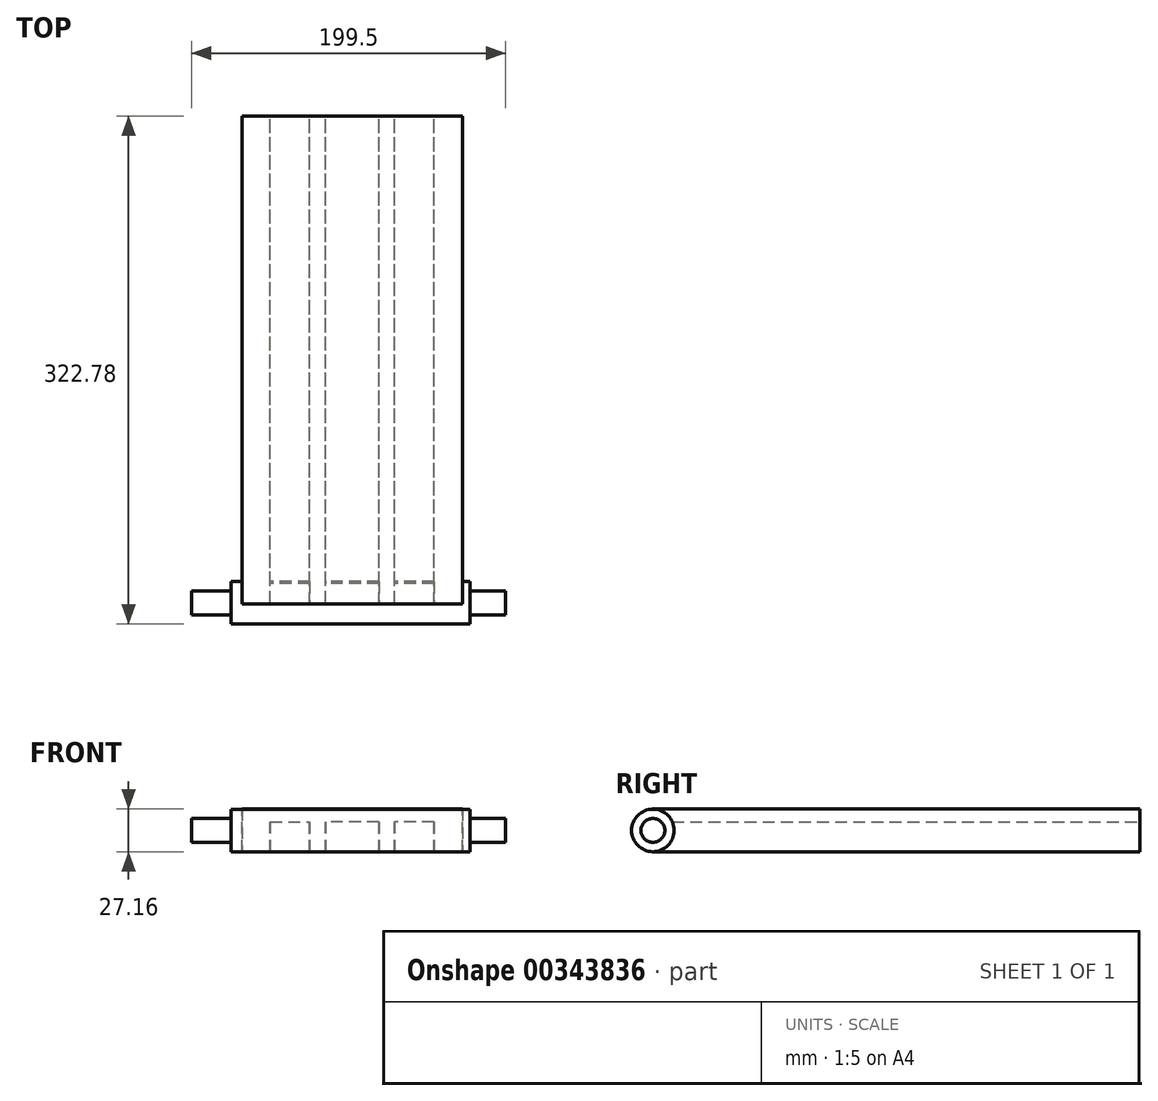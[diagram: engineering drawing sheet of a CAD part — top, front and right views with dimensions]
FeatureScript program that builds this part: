
annotation { "Feature Type Name" : "Feature", "Feature Type Description" : "" }
export const myFeature = defineFeature(function(context is Context, id is Id, definition is map)
    precondition{}
    {
        {
            var Q0;
            Q0=qCreatedBy(makeId("Front.planeOp"),FACE);
            var sketch = newSketch(context, id + "F0", { "sketchPlane" : qUnion([Q0])});
            skLineSegment(sketch, "E0.top", {"start": v(-51.02, -19.16) * mm, "end": v(-69.02, -19.16) * mm});
            skLineSegment(sketch, "E0.left", {"start": v(-51.02, 0) * mm, "end": v(-51.02, -19.16) * mm});
            skLineSegment(sketch, "E0.right", {"start": v(-69.02, 3.84) * mm, "end": v(-69.02, -19.16) * mm});
            skLineSegment(sketch, "E1.top", {"start": v(52.98, -19.16) * mm, "end": v(70.98, -19.16) * mm});
            skLineSegment(sketch, "E1.left", {"start": v(52.98, 0) * mm, "end": v(52.98, -19.16) * mm});
            skLineSegment(sketch, "E1.right", {"start": v(70.98, 3.84) * mm, "end": v(70.98, -19.16) * mm});
            skLineSegment(sketch, "E2.bottom", {"start": v(17.98, 0) * mm, "end": v(-16.02, 0) * mm});
            skLineSegment(sketch, "E3.top", {"start": v(-69.02, 8) * mm, "end": v(70.98, 8) * mm});
            skLineSegment(sketch, "E3.left", {"start": v(-69.02, 3.84) * mm, "end": v(-69.02, 8) * mm});
            skLineSegment(sketch, "E3.right", {"start": v(70.98, 3.84) * mm, "end": v(70.98, 8) * mm});
            skLineSegment(sketch, "E4.0", {"start": v(-26.02, 0) * mm, "end": v(-26.02, -19.16) * mm});
            skLineSegment(sketch, "E5.0", {"start": v(27.98, 0) * mm, "end": v(27.98, -19.16) * mm});
            skLineSegment(sketch, "E6.0", {"start": v(-16.02, 0) * mm, "end": v(-16.02, -19.16) * mm});
            skLineSegment(sketch, "E7.0", {"start": v(17.98, 0) * mm, "end": v(17.98, -19.16) * mm});
            skLineSegment(sketch, "E8", {"start": v(-16.02, -19.16) * mm, "end": v(-26.02, -19.16) * mm});
            skLineSegment(sketch, "E9", {"start": v(17.98, -19.16) * mm, "end": v(27.98, -19.16) * mm});
            skLineSegment(sketch, "E10", {"start": v(52.98, 0) * mm, "end": v(27.98, 0) * mm});
            skLineSegment(sketch, "E11", {"start": v(-51.02, 0) * mm, "end": v(-26.02, 0) * mm});
            skLineSegment(sketch, "E12", {"start": v(-51.02, 0) * mm, "end": v(-51.02, 8) * mm});
            skLineSegment(sketch, "E13", {"start": v(52.98, 0) * mm, "end": v(52.98, 8) * mm});
            skLineSegment(sketch, "E14", {"start": v(-26.02, 0) * mm, "end": v(-26.02, 8) * mm});
            skLineSegment(sketch, "E15", {"start": v(-16.02, 0) * mm, "end": v(-16.02, 8) * mm});
            skLineSegment(sketch, "E16", {"start": v(17.98, 0) * mm, "end": v(17.98, 8) * mm});
            skLineSegment(sketch, "E17", {"start": v(27.98, 0) * mm, "end": v(27.98, 8) * mm});
            skSolve(sketch);
        }
        {
            var Q0;
            Q0=makeQuery(id+"F0.imprint","IMPRINT",FACE,{"disambiguationData":[TD([[makeQuery(id+"F0.imprint","IMPRINT",EDGE,{"derivedFrom":sQuery(id+"F0.wireOp",EDGE,"E1.top")}),1.0]])]});
            var Q1;
            Q1=makeQuery(id+"F0.imprint","IMPRINT",FACE,{"disambiguationData":[TD([[makeQuery(id+"F0.imprint","IMPRINT",EDGE,{"derivedFrom":sQuery(id+"F0.wireOp",EDGE,"E0.top")}),-1.0]])]});
            extrude(context, id + "F1", {"entities" : qUnion([Q0, Q1]), "depth" : 310 * mm});
        }
        {
            var Q0;
            Q0=makeQuery(id+"F0.imprint","IMPRINT",FACE,{"disambiguationData":[TD([[makeQuery(id+"F0.imprint","IMPRINT",EDGE,{"derivedFrom":sQuery(id+"F0.wireOp",EDGE,"E2.bottom")}),-1.0]])]});
            extrude(context, id + "F2", {"entities" : qUnion([Q0]), "depth" : 250 * mm});
        }
        {
            var Q0;
            Q0=makeQuery(id+"F0.imprint","IMPRINT",FACE,{"disambiguationData":[TD([[makeQuery(id+"F0.imprint","IMPRINT",EDGE,{"derivedFrom":sQuery(id+"F0.wireOp",EDGE,"E4.0")}),1.0]])]});
            var Q1;
            Q1=makeQuery(id+"F0.imprint","IMPRINT",FACE,{"disambiguationData":[TD([[makeQuery(id+"F0.imprint","IMPRINT",EDGE,{"derivedFrom":sQuery(id+"F0.wireOp",EDGE,"E5.0")}),-1.0]])]});
            extrude(context, id + "F3", {"entities" : qUnion([Q0, Q1]), "operationType" : NewBodyOperationType.ADD, "depth" : 310 * mm});
        }
        {
            var Q0;
            Q0=makeQuery(id+"F0.imprint","IMPRINT",FACE,{"disambiguationData":[TD([[makeQuery(id+"F0.imprint","IMPRINT",EDGE,{"derivedFrom":sQuery(id+"F0.wireOp",EDGE,"E11")}),1.0]])]});
            var Q1;
            Q1=makeQuery(id+"F0.imprint","IMPRINT",FACE,{"disambiguationData":[TD([[makeQuery(id+"F0.imprint","IMPRINT",EDGE,{"derivedFrom":sQuery(id+"F0.wireOp",EDGE,"E10")}),-1.0]])]});
            var Q2;
            Q2=makeQuery(id+"F0.imprint","IMPRINT",FACE,{"disambiguationData":[TD([[makeQuery(id+"F0.imprint","IMPRINT",EDGE,{"derivedFrom":sQuery(id+"F0.wireOp",EDGE,"E2.bottom")}),-1.0]])]});
            extrude(context, id + "F4", {"entities" : qUnion([Q0, Q1, Q2]), "depth" : 309.9 * mm});
        }
        {
            var Q0;
            Q0=qCreatedBy(makeId("Right.planeOp"),FACE);
            var sketch = newSketch(context, id + "F5", { "sketchPlane" : qUnion([Q0])});
            skCircle(sketch, "E18", {"center": v(-309.28, -5.52) * mm, "radius": 13.5 * mm});
            skPoint(sketch, "E18.first.point", {"position": v(-310.03, 7.96) * mm});
            skPoint(sketch, "E18.second.point", {"position": v(-309.92, -19) * mm});
            skPoint(sketch, "E18.third.point", {"position": v(-313.11, -18.46) * mm});
            skSolve(sketch);
        }
        {
            var Q0;
            Q0=makeQuery(id+"F5.imprint","IMPRINT",FACE,{"disambiguationData":[TD([[makeQuery(id+"F5.imprint","IMPRINT",EDGE,{"derivedFrom":sQuery(id+"F5.wireOp",EDGE,"E18")}),1.0]])]});
            extrude(context, id + "F6", {"entities" : qUnion([Q0]), "operationType" : NewBodyOperationType.ADD, "endBound" : BoundingType.SYMMETRIC, "depth" : 152 * mm});
        }
        {
            var Q0;
            Q0=makeQuery(id+"F6.opExtrude","CAP_FACE",FACE,{"disambiguationData":[OSD([sQuery(id+"F5.wireOp",EDGE,"E18")])],"isStart":false});
            var sketch = newSketch(context, id + "F7", { "sketchPlane" : qUnion([Q0])});
            skCircle(sketch, "E19", {"center": v(-309.28, -5.52) * mm, "radius": 7.58 * mm});
            skSolve(sketch);
        }
        {
            var Q0;
            Q0=makeQuery(id+"F7.imprint","IMPRINT",FACE,{"disambiguationData":[TD([[makeQuery(id+"F7.imprint","IMPRINT",EDGE,{"derivedFrom":sQuery(id+"F7.wireOp",EDGE,"E19")}),1.0]])]});
            extrude(context, id + "F8", {"entities" : qUnion([Q0]), "operationType" : NewBodyOperationType.REMOVE, "oppositeDirection" : true, "depth" : 325 * mm});
        }
        {
            var Q0;
            Q0=makeQuery(id+"F7.imprint","IMPRINT",FACE,{"disambiguationData":[TD([[makeQuery(id+"F7.imprint","IMPRINT",EDGE,{"derivedFrom":sQuery(id+"F7.wireOp",EDGE,"E19")}),1.0]])]});
            extrude(context, id + "F9", {"entities" : qUnion([Q0]), "operationType" : NewBodyOperationType.ADD, "endBound" : BoundingType.SYMMETRIC, "oppositeDirection" : true, "depth" : 354 * mm});
        }
        {
            var Q0;
            Q0=makeQuery(id+"F9.opExtrude","CAP_FACE",FACE,{"disambiguationData":[OSD([sQuery(id+"F7.wireOp",EDGE,"E19")])],"isStart":true});
            extrude(context, id + "F10", {"entities" : qUnion([Q0]), "operationType" : NewBodyOperationType.ADD, "oppositeDirection" : true, "depth" : 162.7 * mm});
        }
        {
            var Q0;
            Q0=makeQuery(id+"F9.opExtrude","CAP_FACE",FACE,{"disambiguationData":[OSD([sQuery(id+"F7.wireOp",EDGE,"E19")])],"isStart":true});
            extrude(context, id + "F11", {"entities" : qUnion([Q0]), "operationType" : NewBodyOperationType.REMOVE, "oppositeDirection" : true, "depth" : 154.5 * mm});
        }
    });
